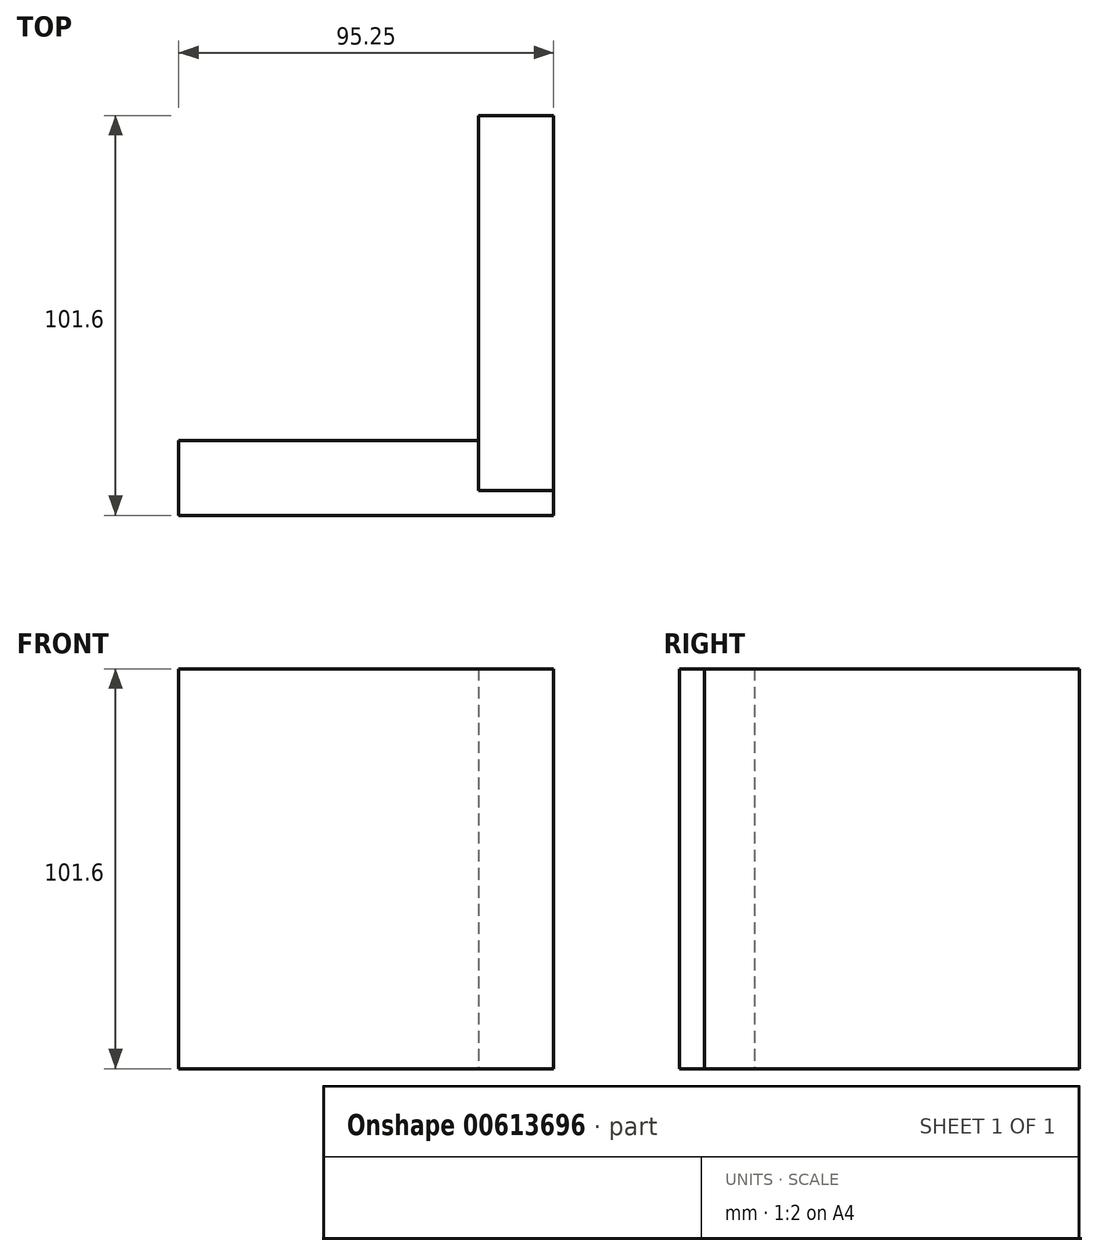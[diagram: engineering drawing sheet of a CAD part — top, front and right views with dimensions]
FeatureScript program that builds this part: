
annotation { "Feature Type Name" : "Feature", "Feature Type Description" : "" }
export const myFeature = defineFeature(function(context is Context, id is Id, definition is map)
    precondition{}
    {
        {
            var Q0;
            Q0=qCreatedBy(makeId("Top.planeOp"),FACE);
            var sketch = newSketch(context, id + "F0", { "sketchPlane" : qUnion([Q0])});
            skLineSegment(sketch, "E0.bottom", {"start": v(0, 0) * mm, "end": v(-76.2, 0) * mm});
            skLineSegment(sketch, "E0.top", {"start": v(0, 19.05) * mm, "end": v(-76.2, 19.05) * mm});
            skLineSegment(sketch, "E0.left", {"start": v(0, 0) * mm, "end": v(0, 19.05) * mm});
            skLineSegment(sketch, "E0.right", {"start": v(-76.2, 0) * mm, "end": v(-76.2, 19.05) * mm});
            skLineSegment(sketch, "E1.bottom", {"start": v(0, 0) * mm, "end": v(19.05, 0) * mm});
            skLineSegment(sketch, "E1.top", {"start": v(0, 101.6) * mm, "end": v(19.05, 101.6) * mm});
            skLineSegment(sketch, "E1.left", {"start": v(0, 0) * mm, "end": v(0, 101.6) * mm});
            skLineSegment(sketch, "E1.right", {"start": v(19.05, 0) * mm, "end": v(19.05, 101.6) * mm});
            skLineSegment(sketch, "E2.top", {"start": v(0, 6.35) * mm, "end": v(19.05, 6.35) * mm});
            skLineSegment(sketch, "E2.left", {"start": v(0, 0) * mm, "end": v(0, 6.35) * mm});
            skLineSegment(sketch, "E2.right", {"start": v(19.05, 0) * mm, "end": v(19.05, 6.35) * mm});
            skSolve(sketch);
        }
        {
            var Q0;
            Q0=makeQuery(id+"F0.imprint","IMPRINT",FACE,{"disambiguationData":[TD([[makeQuery(id+"F0.imprint","IMPRINT",EDGE,{"derivedFrom":sQuery(id+"F0.wireOp",EDGE,"E0.bottom")}),-1.0]])]});
            var Q1;
            Q1=makeQuery(id+"F0.imprint","IMPRINT",FACE,{"disambiguationData":[TD([[makeQuery(id+"F0.imprint","IMPRINT",EDGE,{"derivedFrom":sQuery(id+"F0.wireOp",EDGE,"E1.bottom")}),1.0]])]});
            extrude(context, id + "F1", {"entities" : qUnion([Q0, Q1]), "depth" : 101.6 * mm, "offsetDistance" : 25.4 * mm});
        }
        {
            var Q0;
            {var subQ2=sQuery(id+"F0.wireOp",EDGE,"E1.top");Q0=makeQuery(id+"F0.imprint","IMPRINT",FACE,{"disambiguationData":[TD([[makeQuery(id+"F0.imprint","IMPRINT",EDGE,{"derivedFrom":subQ2}),-1.0]])]});}
            extrude(context, id + "F2", {"entities" : qUnion([Q0]), "depth" : 101.6 * mm, "offsetDistance" : 25.4 * mm});
        }
    });
